# Revit family: R-CVA-0005
name_source: partatom
category: Fenêtres
units: mm (PartAtom-declared; Revit-internal decimal feet)

## family parameters
Couper avec des vides une fois chargée = Non
Hôte = Mur
Partagée = Non
Point de calcul de pièce = Non
Toujours verticalement = Oui

## types (2) — shared parameters
Anti-Effraction = RESISTANCE AUX CHOCS : 2B2 (900J) (selon NF EN 12600))
Applique = Non
Construction analytique = <Aucun>
Fabricant = MONTIBERT
Huisserie_Delardage Largeur = 8 mm  [stored 0.0262467 ft]
Huisserie_Délardage Bas Epaisseur = 8 mm  [stored 0.0262467 ft]
Huisserie_Délardage Haut  Epaisseur = 8 mm  [stored 0.0262467 ft]
Huisserie_Délardage_Bas = Non
Huisserie_Délardage_Haut = Non
Huisserie_Feuillure Epaisseur = 40 mm  [stored 0.131234 ft]
Huisserie_Feuillure Largeur = 24 mm  [stored 0.0787402 ft]
Huisserie_Feuillure_Basse = Non
Huisserie_Matériau = Hêtre
Huisserie_Profil_Epaisseur = 118 mm  [stored 0.387139 ft]
Huisserie_Rainure à Brique = Non
Huisserie_Rainure à Brique_Largeur = 8 mm  [stored 0.0262467 ft]
Materiaux_Dominant = Bois
Modèle = 05 - Châssis Vitré
Montant_1 = Non
Montant_2 = Non
Montant_Largeur = 72 mm  [stored 0.23622 ft]
Parclosage à Recouvrement = Non
Parclose Jeu Epaisseur = 1 mm  [stored 0.00328084 ft]
Parclose Largeur = 24 mm  [stored 0.0787402 ft]
Parclose Recouvrement Epaisseur = 6 mm  [stored 0.019685 ft]
Parclose Recouvrement Largeur = 6 mm  [stored 0.019685 ft]
Parcloses_Matériau = Hêtre
Profil 1_Largeur = 50 mm  [stored 0.164042 ft]
Profil 1_Latéral = Non
Profil 2_Largeur = 50 mm  [stored 0.164042 ft]
Profil 2_Latéral = Non
Profil Bas = Non
Profil Bas_Largeur = 70 mm  [stored 0.229659 ft]
Profil Haut = Non
Profil Haut_Largeur = 50 mm  [stored 0.164042 ft]
Profil_Délardage_Bas_Epaisseur = 8 mm  [stored 0.0262467 ft]
Profil_Délardage_Haut_Epaisseur = 8 mm  [stored 0.0262467 ft]
Profil_Délardage_Largeur = 8 mm  [stored 0.0262467 ft]
Profil_Déplacement Vers Nu Ext = Non
Profil_Déplacement Vers Nu Int = Oui
Profil_Déplacement Vers l'Huisserie = Oui
Profil_Déplacement Vers le Mur = Non
Profil_Matériau = Hêtre
Profil_Rainure à Brique_ coté Ext = Non
Profil_Rainure à Brique_ coté Int = Oui
Profils_Délardage Bas_coté Ext = Non
Profils_Délardage Bas_coté Int = Non
Profils_Délardage Haut_coté Ext = Non
Profils_Délardage Haut_coté Int = Non
Profils_Déplacement X = 8 mm  [stored 0.0262467 ft]
Profils_Déplacement Y' = 8 mm  [stored 0.0262467 ft]
Recouvrement = Non
Reference_Commerciale = C EW30 VAc
Resistance_Feu = E30-EW130
Sens_Feu = Recto / Verso
Tunnel = Oui
URL = https://www.malerba.fr
Vitrage Epaisseur = 16 mm  [stored 0.0524934 ft]
Vitrage_Matériau = Verre
X_Ambrasure Décalage Epaisseur = 8 mm  [stored 0.0262467 ft]
zero-valued in all types: Ambrasure, Jeu Bas, Jeu Haut, Jeu Latéral 1, Jeu Latéral 2, Parclose Jeu Largeur, Profils_Déplacement X', Profils_Déplacement Y, X3'_Déduction Délardages Profils, X3_Déduction Délardages Profils, X4'_Déduction Délardages Huisseries, X4_Déduction Délardages Huisseries, X_Ambrasure, X_Huisserie Décalage Hauteur, X_Huisserie Décalage Hauteur_INV, X_Huisserie Décalage Largeur, X_Huisserie Décalage Largeur_INV, X_Huisserie_Delardage Largeur, X_Profil 1_Largeur, X_Profil 2_Largeur, X_Profil Bas_Largeur, X_Profil Haut_Largeur, X_Profil_Délardage_Largeur

## per-type parameters (varying)
| type | Acoustique | Châssis Hauteur Hors Tout | Châssis Largeur Hors Tout | Code_MAJ | Description | Fiche_Produit | Huisserie_Feuillure_Haute | Huisserie_Feuillure_Sans | Huisserie_Profil_Largeur | Note d'identification | X1'_Tunnel | X1_Tunnel | X2'_Recouvrement et Applique | X2_Recouvrement et Applique | X_Ouvertur Mur Largeur | X_Ouverture Mur Hauteur |
| CVA-0005 | Rw (C ; Ctr) = 38 (-1 ; -3) dB | 577 mm | 1141 mm  [stored 3.74344 ft] | 2019102206CVA0005 | Chassis vitré grande surface, EW30, 38(-1; -3) dB (performance du vitrage), résistance aux chocs 1B1, vitrage résistant aux UV, avec parcloses bois, sur cadre bois | CVA-0005 | Oui | Non | 58 mm | CHASSIS VITRE EW30 - GRANDE SURFACE | 577 mm | 1141 mm  [stored 3.74344 ft] | 577 mm | 1141 mm  [stored 3.74344 ft] | 1141 mm  [stored 3.74344 ft] | 577 mm |
| CVA-0001 579 | Rw (C ; Ctr) = 37 (-1 ; -3) dB | 579 mm | 1140 mm | 2019102206CVA0001 | Chassis vitré, EW30, 37(-1; -3) dB (performance du vitrage), résistance aux chocs 2B2, sans résistance aux UV, avec parcloses bois, sur cadre bois | CVA-0001 | Non | Oui | 56 mm  [stored 0.183727 ft] | CHASSIS VITRE EW30 | 579 mm | 1140 mm | 579 mm | 1140 mm | 1140 mm | 579 mm |

note: [stored X ft] marks values corroborated as IEEE doubles in the binary element streams (Revit-internal decimal feet)

## geometry (parser evidence)
native form markers: Blend x24
no freeform markers — native parametric forms only
